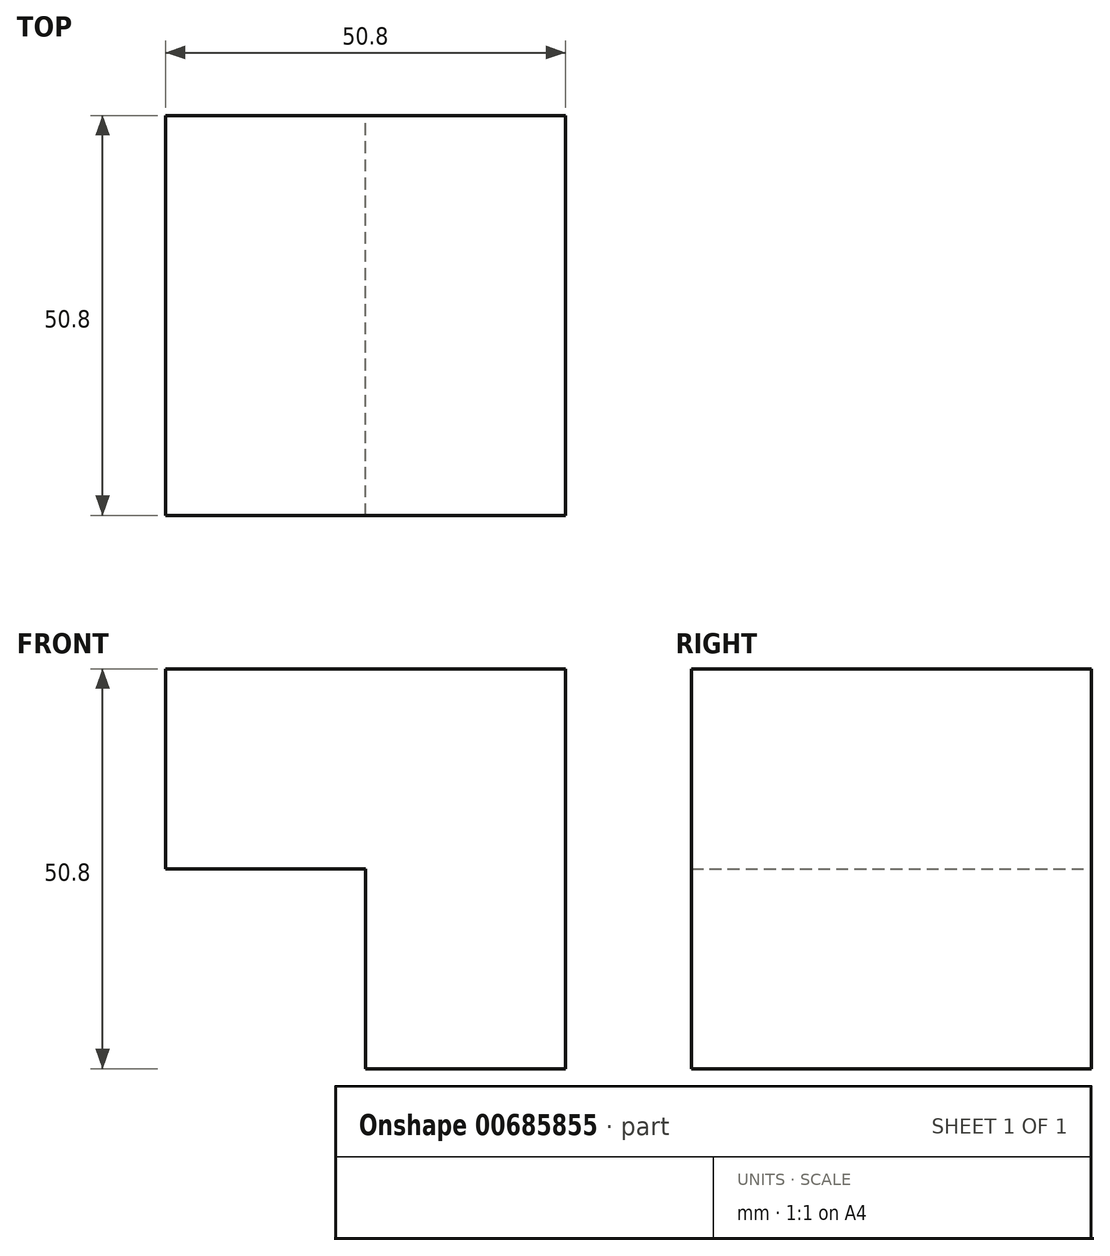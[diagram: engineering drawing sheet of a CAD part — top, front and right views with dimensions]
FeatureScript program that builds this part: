
annotation { "Feature Type Name" : "Feature", "Feature Type Description" : "" }
export const myFeature = defineFeature(function(context is Context, id is Id, definition is map)
    precondition{}
    {
        {
            var Q0;
            Q0=qCreatedBy(makeId("Front.planeOp"),FACE);
            var sketch = newSketch(context, id + "F0", { "sketchPlane" : qUnion([Q0])});
            skLineSegment(sketch, "E0", {"start": v(-8.5, 64.26) * mm, "end": v(-59.3, 64.26) * mm});
            skLineSegment(sketch, "E1", {"start": v(-8.5, 64.26) * mm, "end": v(-8.5, 13.46) * mm});
            skLineSegment(sketch, "E2", {"start": v(-8.5, 13.46) * mm, "end": v(-33.9, 13.46) * mm});
            skLineSegment(sketch, "E3", {"start": v(-33.9, 13.46) * mm, "end": v(-33.9, 38.86) * mm});
            skLineSegment(sketch, "E4", {"start": v(-33.9, 38.86) * mm, "end": v(-59.3, 38.86) * mm});
            skLineSegment(sketch, "E5.trimOffspring", {"start": v(-59.3, 38.86) * mm, "end": v(-59.3, 64.26) * mm});
            skPoint(sketch, "E6.start.orphan", {"position": v(-59.3, 13.46) * mm});
            skSolve(sketch);
        }
        {
            var Q0;
            Q0=makeQuery(id+"F0.imprint","IMPRINT",FACE,{"disambiguationData":[TD([[makeQuery(id+"F0.imprint","IMPRINT",EDGE,{"derivedFrom":sQuery(id+"F0.wireOp",EDGE,"E0")}),1.0]])]});
            extrude(context, id + "F1", {"entities" : qUnion([Q0]), "depth" : 50.8 * mm, "offsetDistance" : 25.4 * mm});
        }
    });
